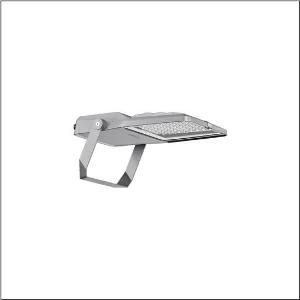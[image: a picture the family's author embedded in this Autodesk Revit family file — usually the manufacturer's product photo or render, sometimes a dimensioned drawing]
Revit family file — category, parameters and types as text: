
# Revit family: floodlight_fl_21_iq_mini___pl64_5xa7772c5e1a_f6c6
name_source: partatom
category: Lighting Fixtures
units: mm (PartAtom-declared; Revit-internal decimal feet)

## family parameters
Cut with Voids When Loaded = No
Host = Face
Light Source = No
Part Type = Normal
Room Calculation Point = No
Round Connector Dimension = Use Diameter
Shared = No

## types (1)
- --- (1 x LED, 11000 lm, 87.2 W, 4000K)
    Apparent Load = 87 VA
    CIE Flux Codes = 28 80 98 100 100
    Color Rendering = 80
    Color Temperature = 4000K
    Default Elevation = 1800 mm
    Description = Floodlight FL 21 iQ mini, floodlight, primary light control with lens, of PMMA, primary optical cover: protective disc, of toughened safety glass, transparent, light distribution: PL64, light emission: direct distribution, installation type: surface-mounted, LED, High Power LED, rated luminous flux: 11.000lm, luminous efficacy: 126lm/W, light colour: 840, colour temperature: 4000K, control: Street-Remote, Auto-Match, Temp-Guard, Night-Set, Smart-Wire, Desk-Remote (wireless, voltage-free reading and setting of iQ features in the workshop via application-optimized NFC function/RFID function), optimised constant luminous flux control (CLO 2.0), with terminal, 6-pole, mains connection: 220..240V, AC, 50/60Hz, start of lifetime: 87W, end of service life: 92W, reduction: 40W, luminaire housing, of diecast aluminium, powder-coated, Siteco® metallic grey (DB 702S), corrosivity category C5 mid according to DIN EN ISO 12944, sealing non-destructively replaceable, mounting bracket, of steel, galvanised, powder-coated, Siteco® metallic grey (DB 702S), protection rating (complete): IP66, insulation class (complete): insulation class II (safety insulation), certification: CE, ENEC, VDE, protection symbol: D, impact resistance: IK08, permissible operating ambient temperature: -40..+40°C, permissible operating ambient temperature for outdoor applications: -40..+50°C, standard: DIN EN 12944, LABS conformity tested according to VDMA 24364:2018-05, packaging unit: 1 piece

Light Distribution: PL64
    Height = 70 mm
    Lamp = 1 x LED
    Lamp Light Flux = 11000 lm
    Lamp Power = 87.2 W
    Lamp count = 1
    Length = 485 mm
    Luminous efficacy = 126 lm/W
    Manufacturer = Siteco
    ModVariant = No
    Model = 5XA7772C5E1A
    Number of Poles = 1
    OnlyDefault = Yes
    Power Factor = 1
    Product Name = Floodlight FL 21 iQ mini | PL64
    Product group = floodlight | pylon annexe
    ProductGroupID = 6200
    Protection Class = Protection class II
    Protection Degree = IP 66
    RLX_Detail_Level = 1
    RLX_Emergency_Light_Flux = 0 lm
    RLX_Emergency_Type = 0
    RLX_Emergency_Type_DB = No
    RlxData = <blob elided: 96349 chars, md5=d34f66a8>
    Socket = socket
    Standby Power = 0 W
    System Light Flux = 11000 lm
    System Power = 87 W
    Type Comments = factory setting: luminous flux: 100 % | dim-lin: 254 | 456 mA
    Type Image = l_1006845.jpg
    URL = http://relux.com
    VarID = @adj_098481
    Voltage = 0 V
    Weight = 0.00 kg
    Width = 337 mm

## geometry (parser evidence)
native form markers: Blend x4, Sweep x11
no freeform markers — native parametric forms only
